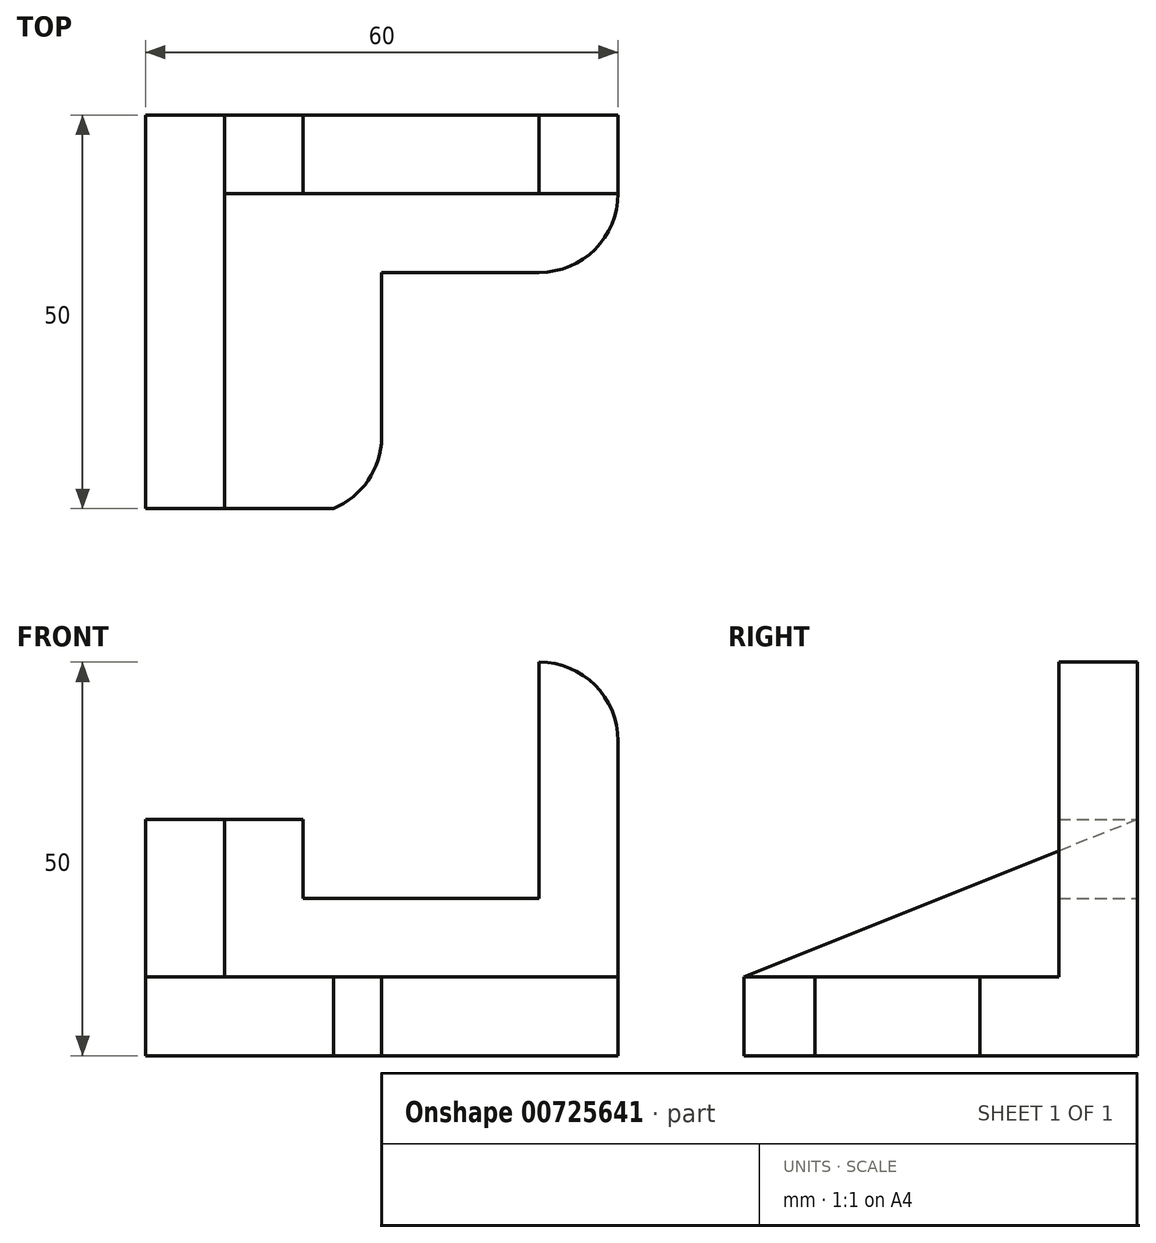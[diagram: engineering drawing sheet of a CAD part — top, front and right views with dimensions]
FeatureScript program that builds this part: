
annotation { "Feature Type Name" : "Feature", "Feature Type Description" : "" }
export const myFeature = defineFeature(function(context is Context, id is Id, definition is map)
    precondition{}
    {
        {
            var Q0;
            Q0=qCreatedBy(makeId("Front.planeOp"),FACE);
            var sketch = newSketch(context, id + "F0", { "sketchPlane" : qUnion([Q0])});
            skLineSegment(sketch, "E0", {"start": v(0, 0) * mm, "end": v(60, 0) * mm});
            skLineSegment(sketch, "E1", {"start": v(60, 0) * mm, "end": v(60, 50) * mm});
            skLineSegment(sketch, "E2", {"start": v(60, 50) * mm, "end": v(50, 50) * mm});
            skLineSegment(sketch, "E3", {"start": v(50, 50) * mm, "end": v(50, 20) * mm});
            skLineSegment(sketch, "E4", {"start": v(50, 20) * mm, "end": v(20, 20) * mm});
            skLineSegment(sketch, "E5", {"start": v(20, 20) * mm, "end": v(20, 30) * mm});
            skLineSegment(sketch, "E6", {"start": v(20, 30) * mm, "end": v(0, 30) * mm});
            skLineSegment(sketch, "E7", {"start": v(0, 30) * mm, "end": v(0, 0) * mm});
            skSolve(sketch);
        }
        {
            var Q0;
            Q0=makeQuery(id+"F0.imprint","IMPRINT",FACE,{"disambiguationData":[TD([[makeQuery(id+"F0.imprint","IMPRINT",EDGE,{"derivedFrom":sQuery(id+"F0.wireOp",EDGE,"E0")}),1.0]])]});
            extrude(context, id + "F1", {"entities" : qUnion([Q0]), "depth" : 50 * mm, "offsetDistance" : 25 * mm});
        }
        {
            var Q0;
            Q0=makeQuery(id+"F1.opExtrude","CAP_FACE",FACE,{"disambiguationData":[OSD([sQuery(id+"F0.wireOp",EDGE,"E0"),sQuery(id+"F0.wireOp",EDGE,"E1"),sQuery(id+"F0.wireOp",EDGE,"E2"),sQuery(id+"F0.wireOp",EDGE,"E3"),sQuery(id+"F0.wireOp",EDGE,"E4"),sQuery(id+"F0.wireOp",EDGE,"E5"),sQuery(id+"F0.wireOp",EDGE,"E6"),sQuery(id+"F0.wireOp",EDGE,"E7")])],"isStart":false});
            var sketch = newSketch(context, id + "F2", { "sketchPlane" : qUnion([Q0])});
            skLineSegment(sketch, "E8", {"start": v(0, 0) * mm, "end": v(0, 10) * mm});
            skLineSegment(sketch, "E9", {"start": v(0, 10) * mm, "end": v(60, 10) * mm});
            skLineSegment(sketch, "E10", {"start": v(60, 10) * mm, "end": v(60, 20) * mm});
            skLineSegment(sketch, "E11", {"start": v(60, 20) * mm, "end": v(10, 20) * mm});
            skLineSegment(sketch, "E12", {"start": v(10, 20) * mm, "end": v(10, 10) * mm});
            skSolve(sketch);
        }
        {
            var Q0;
            {var subQ3=sQuery(id+"F2.wireOp",EDGE,"E10");Q0=makeQuery(id+"F2.imprint","IMPRINT",FACE,{"disambiguationData":[TD([[makeQuery(id+"F2.imprint","IMPRINT",EDGE,{"derivedFrom":subQ3}),1.0]])]});}
            extrude(context, id + "F3", {"entities" : qUnion([Q0]), "operationType" : NewBodyOperationType.REMOVE, "oppositeDirection" : true, "depth" : 40 * mm, "offsetDistance" : 25 * mm});
        }
        {
            var Q0;
            {var subQ0=sQuery(id+"F0.wireOp",EDGE,"E5");var subQ1=sQuery(id+"F0.wireOp",EDGE,"E6");var subQ2=sQuery(id+"F0.wireOp",EDGE,"E1");var subQ3=sQuery(id+"F0.wireOp",EDGE,"E0");var subQ4=sQuery(id+"F0.wireOp",EDGE,"E7");Q0=makeQuery(id+"F3.boolean.opBoolean","SPLIT",FACE,{"disambiguationData":[TD([makeQuery(id+"F1.opExtrude","SWEPT_FACE",FACE,{"disambiguationData":[OSD([subQ3])]})])],"derivedFrom":makeQuery(id+"F1.opExtrude","CAP_FACE",FACE,{"disambiguationData":[OSD([subQ3,subQ2,sQuery(id+"F0.wireOp",EDGE,"E2"),sQuery(id+"F0.wireOp",EDGE,"E3"),sQuery(id+"F0.wireOp",EDGE,"E4"),subQ0,subQ1,subQ4])],"isStart":false})});}
            var sketch = newSketch(context, id + "F4", { "sketchPlane" : qUnion([Q0])});
            skLineSegment(sketch, "E13", {"start": v(10, 20) * mm, "end": v(10, 30) * mm});
            skSolve(sketch);
        }
        {
            var Q0;
            {var subQ0=sQuery(id+"F4.wireOp",EDGE,"E13");Q0=makeQuery(id+"F4.imprint","IMPRINT",FACE,{"disambiguationData":[TD([[makeQuery(id+"F4.imprint","IMPRINT",EDGE,{"derivedFrom":subQ0}),-1.0]])]});}
            extrude(context, id + "F5", {"entities" : qUnion([Q0]), "operationType" : NewBodyOperationType.REMOVE, "oppositeDirection" : true, "depth" : 40 * mm, "offsetDistance" : 25 * mm});
        }
        {
            var Q0;
            Q0=makeQuery(id+"F1.opExtrude","SWEPT_FACE",FACE,{"disambiguationData":[OSD([sQuery(id+"F0.wireOp",EDGE,"E7")])]});
            var sketch = newSketch(context, id + "F6", { "sketchPlane" : qUnion([Q0])});
            skLineSegment(sketch, "E14", {"start": v(50, 0) * mm, "end": v(50, 10) * mm});
            skLineSegment(sketch, "E15", {"start": v(50, 10) * mm, "end": v(0, 10) * mm});
            skLineSegment(sketch, "E16", {"start": v(0, 10) * mm, "end": v(0, 30) * mm});
            skLineSegment(sketch, "E17", {"start": v(0, 30) * mm, "end": v(50, 10) * mm});
            skSolve(sketch);
        }
        {
            var Q0;
            {var subQ0=sQuery(id+"F6.wireOp",EDGE,"E17");Q0=makeQuery(id+"F6.imprint","IMPRINT",FACE,{"disambiguationData":[TD([[makeQuery(id+"F6.imprint","IMPRINT",EDGE,{"derivedFrom":subQ0}),1.0]])]});}
            extrude(context, id + "F7", {"entities" : qUnion([Q0]), "operationType" : NewBodyOperationType.REMOVE, "oppositeDirection" : true, "depth" : 10 * mm, "offsetDistance" : 25 * mm});
        }
        {
            var Q0;
            Q0=makeQuery(id+"F1.opExtrude","SWEPT_FACE",FACE,{"disambiguationData":[OSD([sQuery(id+"F0.wireOp",EDGE,"E1")])]});
            var sketch = newSketch(context, id + "F8", { "sketchPlane" : qUnion([Q0])});
            skLineSegment(sketch, "E18", {"start": v(-10, 20) * mm, "end": v(-10, 50) * mm});
            skSolve(sketch);
        }
        {
            var Q0;
            {var subQ0=sQuery(id+"F8.wireOp",EDGE,"E18");Q0=makeQuery(id+"F8.imprint","IMPRINT",FACE,{"disambiguationData":[TD([[makeQuery(id+"F8.imprint","IMPRINT",EDGE,{"derivedFrom":subQ0}),1.0]])]});}
            extrude(context, id + "F9", {"entities" : qUnion([Q0]), "operationType" : NewBodyOperationType.REMOVE, "oppositeDirection" : true, "depth" : 40 * mm, "offsetDistance" : 25 * mm});
        }
        {
            var Q0;
            {var subQ0=sQuery(id+"F2.wireOp",EDGE,"E11");Q0=makeQuery(id+"F9.boolean.opBoolean","MERGE",FACE,{"derivedFrom":[makeQuery(id+"F5.boolean.opBoolean","MERGE",FACE,{"derivedFrom":[makeQuery(id+"F3.boolean.opBoolean","COPY",FACE,{"derivedFrom":makeQuery(id+"F3.opExtrude","CAP_FACE",FACE,{"disambiguationData":[OSD([sQuery(id+"F2.wireOp",EDGE,"E9"),sQuery(id+"F2.wireOp",EDGE,"E10"),subQ0,sQuery(id+"F2.wireOp",EDGE,"E12")])],"isStart":false})}),makeQuery(id+"F5.opExtrude","CAP_FACE",FACE,{"disambiguationData":[OSD([sQuery(id+"F0.wireOp",EDGE,"E5"),sQuery(id+"F0.wireOp",EDGE,"E6"),subQ0,sQuery(id+"F4.wireOp",EDGE,"E13")])],"isStart":false})]}),makeQuery(id+"F9.opExtrude","SWEPT_FACE",FACE,{"disambiguationData":[OSD([sQuery(id+"F8.wireOp",EDGE,"E18")])]})]});}
            var sketch = newSketch(context, id + "F10", { "sketchPlane" : qUnion([Q0])});
            skArc(sketch, "E19", {"start": v(60, 40) * mm, "mid": v(57.07, 47.07) * mm, "end": v(50, 50) * mm});
            skSolve(sketch);
        }
        {
            var Q0;
            {var subQ0=sQuery(id+"F10.wireOp",EDGE,"E19");Q0=makeQuery(id+"F10.imprint","IMPRINT",FACE,{"disambiguationData":[TD([[makeQuery(id+"F10.imprint","IMPRINT",EDGE,{"derivedFrom":subQ0}),-1.0]])]});}
            extrude(context, id + "F11", {"entities" : qUnion([Q0]), "operationType" : NewBodyOperationType.REMOVE, "oppositeDirection" : true, "depth" : 25 * mm, "offsetDistance" : 25 * mm});
        }
        {
            var Q0;
            Q0=makeQuery(id+"F3.boolean.opBoolean","COPY",FACE,{"derivedFrom":makeQuery(id+"F3.opExtrude","SWEPT_FACE",FACE,{"disambiguationData":[OSD([sQuery(id+"F2.wireOp",EDGE,"E9")])]})});
            var sketch = newSketch(context, id + "F12", { "sketchPlane" : qUnion([Q0])});
            skLineSegment(sketch, "E20", {"start": v(60, -10) * mm, "end": v(60, -20) * mm});
            skLineSegment(sketch, "E21", {"start": v(60, -20) * mm, "end": v(30, -20) * mm});
            skLineSegment(sketch, "E22", {"start": v(30, -20) * mm, "end": v(30, -50) * mm});
            skLineSegment(sketch, "E23", {"start": v(30, -50) * mm, "end": v(10, -50) * mm});
            skSolve(sketch);
        }
        {
            var Q0;
            {var subQ0=sQuery(id+"F12.wireOp",EDGE,"E21");Q0=makeQuery(id+"F12.imprint","IMPRINT",FACE,{"disambiguationData":[TD([[makeQuery(id+"F12.imprint","IMPRINT",EDGE,{"derivedFrom":subQ0}),1.0]])]});}
            extrude(context, id + "F13", {"entities" : qUnion([Q0]), "operationType" : NewBodyOperationType.REMOVE, "oppositeDirection" : true, "depth" : 10 * mm, "offsetDistance" : 25 * mm});
        }
        {
            var Q0;
            Q0=makeQuery(id+"F3.boolean.opBoolean","COPY",FACE,{"derivedFrom":makeQuery(id+"F3.opExtrude","SWEPT_FACE",FACE,{"disambiguationData":[OSD([sQuery(id+"F2.wireOp",EDGE,"E9")])]})});
            var sketch = newSketch(context, id + "F14", { "sketchPlane" : qUnion([Q0])});
            skArc(sketch, "E24", {"start": v(50, -20) * mm, "mid": v(57.07, -17.07) * mm, "end": v(60, -10) * mm});
            skArc(sketch, "E25", {"start": v(23.86, -50) * mm, "mid": v(28.39, -46.22) * mm, "end": v(30, -40.55) * mm});
            skSolve(sketch);
        }
        {
            var Q0;
            {var subQ0=sQuery(id+"F14.wireOp",EDGE,"E24");Q0=makeQuery(id+"F14.imprint","IMPRINT",FACE,{"disambiguationData":[TD([[makeQuery(id+"F14.imprint","IMPRINT",EDGE,{"derivedFrom":subQ0}),-1.0]])]});}
            var Q1;
            {var subQ0=sQuery(id+"F14.wireOp",EDGE,"E25");var subQ1=makeQuery(id+"F3.boolean.opBoolean","COPY",EDGE,{"derivedFrom":makeQuery(id+"F3.opExtrude","CAP_EDGE",EDGE,{"disambiguationData":[OSD([sQuery(id+"F2.wireOp",EDGE,"E9")])],"isStart":true})});var subQ2=makeQuery(id+"F14.imprint","INTERSECT",VERTEX,{"derivedFrom":[subQ1,subQ0]});Q1=makeQuery(id+"F14.imprint","IMPRINT",FACE,{"disambiguationData":[TD([[makeQuery(id+"F14.imprint","IMPRINT",EDGE,{"disambiguationData":[TD([[subQ2,-1.0]])],"derivedFrom":subQ0}),-1.0]])]});}
            extrude(context, id + "F15", {"entities" : qUnion([Q0, Q1]), "operationType" : NewBodyOperationType.REMOVE, "oppositeDirection" : true, "depth" : 10 * mm, "offsetDistance" : 25 * mm});
        }
    });
